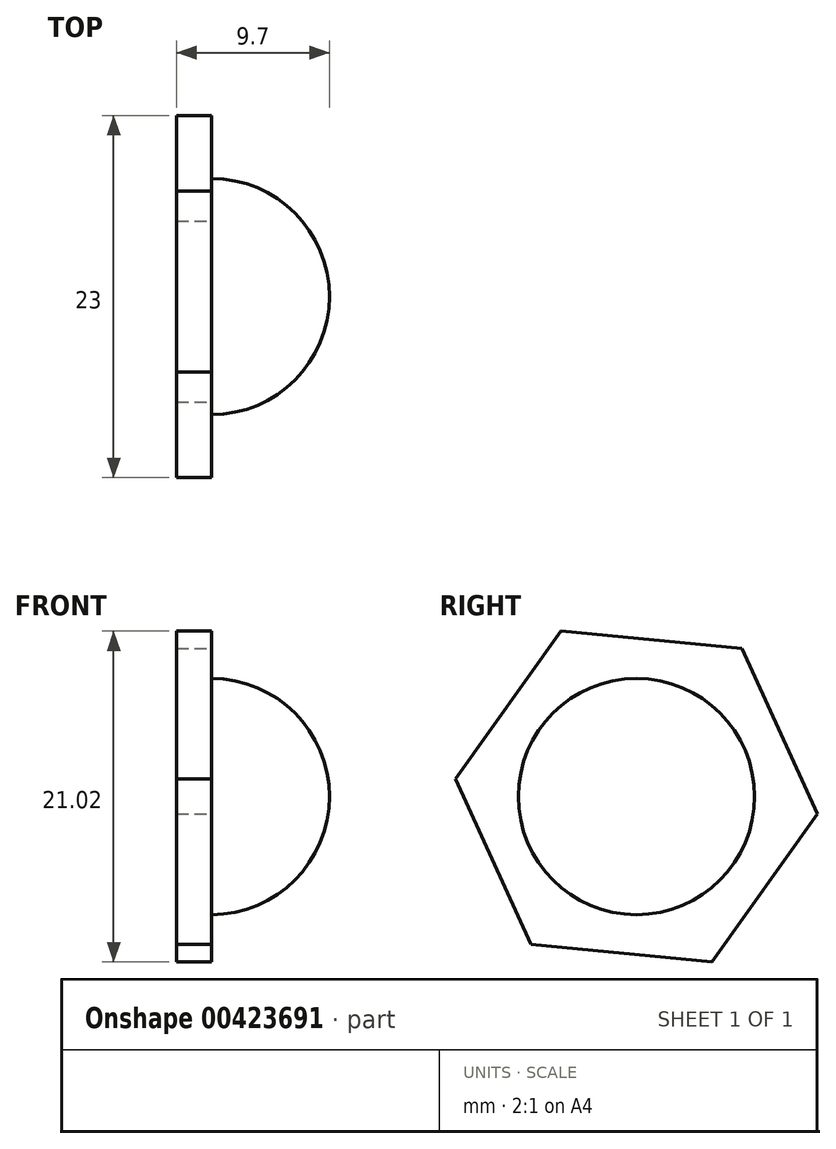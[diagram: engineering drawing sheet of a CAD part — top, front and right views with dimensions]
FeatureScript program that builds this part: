
annotation { "Feature Type Name" : "Feature", "Feature Type Description" : "" }
export const myFeature = defineFeature(function(context is Context, id is Id, definition is map)
    precondition{}
    {
        {
            var Q0;
            Q0=qCreatedBy(makeId("Right.planeOp"),FACE);
            var sketch = newSketch(context, id + "F0", { "sketchPlane" : qUnion([Q0])});
            skLineSegment(sketch, "E0", {"start": v(0, 7.5) * mm, "end": v(0, -7.5) * mm});
            skArc(sketch, "E1", {"start": v(0, -7.5) * mm, "mid": v(7.5, 0) * mm, "end": v(0, 7.5) * mm});
            skSolve(sketch);
        }
        {
            var Q0;
            Q0=makeQuery(id+"F0.imprint","IMPRINT",FACE,{"disambiguationData":[TD([[makeQuery(id+"F0.imprint","IMPRINT",EDGE,{"derivedFrom":sQuery(id+"F0.wireOp",EDGE,"E0")}),1.0]])]});
            var Q1;
            Q1=sQuery(id+"F0.wireOp",EDGE,"E0");
            revolve(context, id + "F1", {"entities" : qUnion([Q0]), "axis" : qUnion([Q1]), "revolveType" : RevolveType.ONE_DIRECTION, "angle" : 180 * degree});
        }
        {
            var Q0;
            Q0=qCreatedBy(makeId("Right.planeOp"),FACE);
            var sketch = newSketch(context, id + "F2", { "sketchPlane" : qUnion([Q0])});
            skCircle(sketch, "E2.cCircle", {"center": v(0, 0) * mm, "radius": 10 * mm, "construction": true});
            skLineSegment(sketch, "E2.0", {"start": v(-11.5, 1.11) * mm, "end": v(-4.79, 10.51) * mm});
            skLineSegment(sketch, "E2.1", {"start": v(-4.79, 10.51) * mm, "end": v(6.71, 9.4) * mm});
            skLineSegment(sketch, "E2.2", {"start": v(6.71, 9.4) * mm, "end": v(11.5, -1.11) * mm});
            skLineSegment(sketch, "E2.3", {"start": v(11.5, -1.11) * mm, "end": v(4.79, -10.51) * mm});
            skLineSegment(sketch, "E2.4", {"start": v(4.79, -10.51) * mm, "end": v(-6.71, -9.4) * mm});
            skLineSegment(sketch, "E2.5", {"start": v(-6.71, -9.4) * mm, "end": v(-11.5, 1.11) * mm});
            skPoint(sketch, "E2.0.midPoint", {"position": v(-8.14, 5.81) * mm});
            skSolve(sketch);
        }
        {
            var Q0;
            Q0=makeQuery(id+"F2.imprint","IMPRINT",FACE,{"disambiguationData":[TD([[makeQuery(id+"F2.imprint","IMPRINT",EDGE,{"derivedFrom":sQuery(id+"F2.wireOp",EDGE,"E2.0")}),-1.0]])]});
            extrude(context, id + "F3", {"entities" : qUnion([Q0]), "operationType" : NewBodyOperationType.ADD, "oppositeDirection" : true, "depth" : 2.2 * mm});
        }
    });
